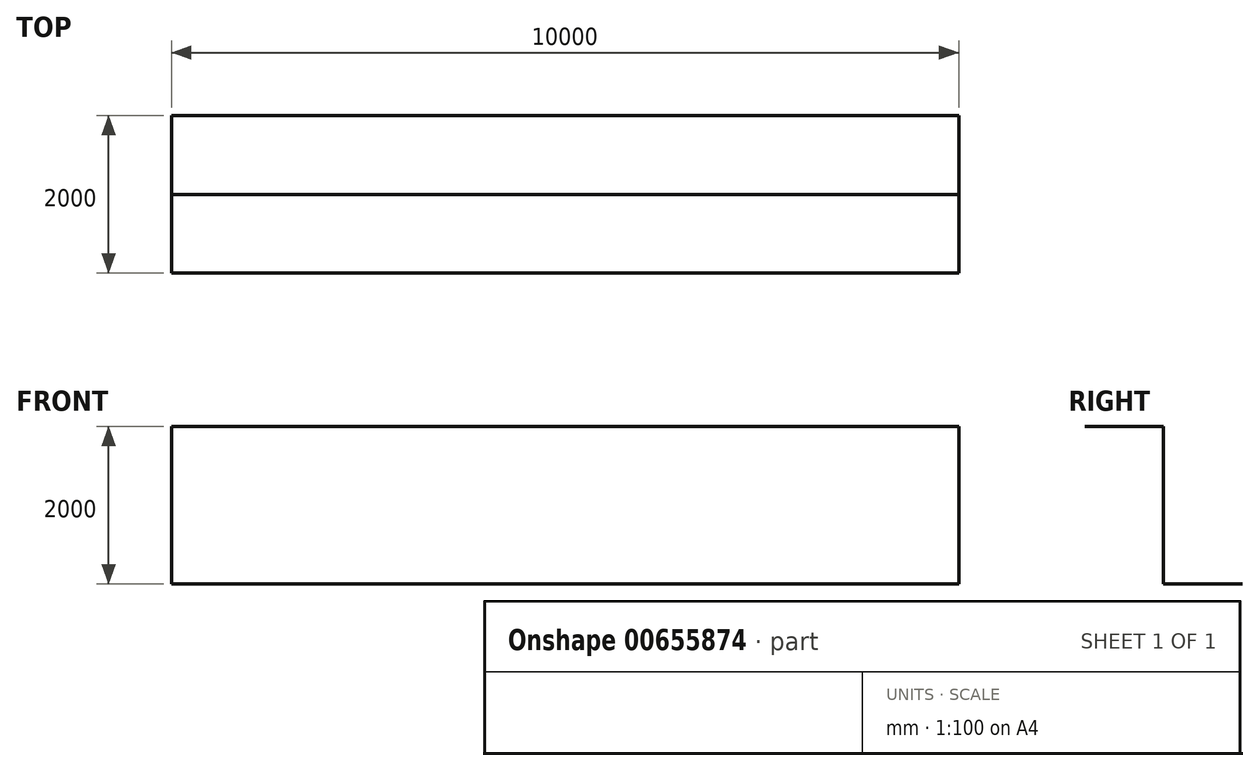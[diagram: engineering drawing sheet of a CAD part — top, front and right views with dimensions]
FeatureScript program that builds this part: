
annotation { "Feature Type Name" : "Feature", "Feature Type Description" : "" }
export const myFeature = defineFeature(function(context is Context, id is Id, definition is map)
    precondition{}
    {
        {
            var Q0;
            Q0=qCreatedBy(makeId("Right.planeOp"),FACE);
            var sketch = newSketch(context, id + "F0", { "sketchPlane" : qUnion([Q0])});
            skLineSegment(sketch, "E0", {"start": v(0, 0) * mm, "end": v(0, 1000) * mm});
            skLineSegment(sketch, "E1", {"start": v(0, 1000) * mm, "end": v(-1000, 1000) * mm});
            skLineSegment(sketch, "E2", {"start": v(0, 0) * mm, "end": v(0, -1000) * mm});
            skLineSegment(sketch, "E3", {"start": v(0, -1000) * mm, "end": v(1000, -1000) * mm});
            skSolve(sketch);
        }
        {
            var Q0;
            Q0 = qSketchRegion(id + "F0", true);
            var Q1;
            Q1 = qConstructionFilter(qBodyType(qCreatedBy(id + "F0" ,EDGE), BodyType.WIRE), ConstructionObject.NO);
            extrude(context, id + "F1", {"entities" : qUnion([Q0]), "bodyType" : ToolBodyType.SURFACE, "surfaceEntities" : qUnion([Q1]), "depth" : 10000 * mm, "offsetDistance" : 25 * mm});
        }
    });
